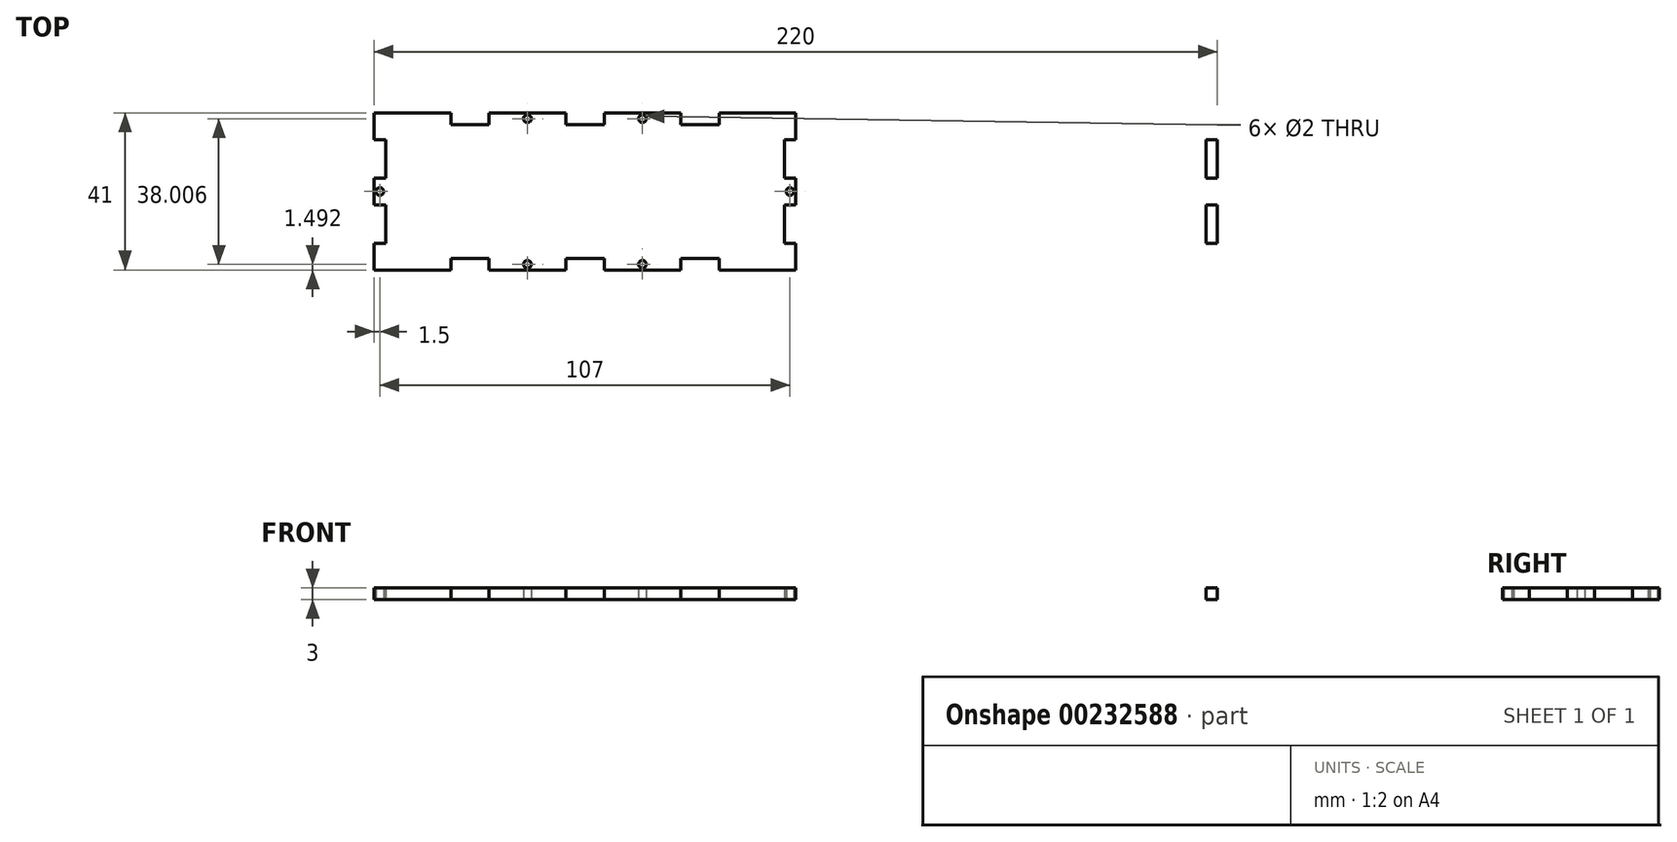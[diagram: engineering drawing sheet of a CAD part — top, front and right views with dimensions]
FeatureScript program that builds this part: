
annotation { "Feature Type Name" : "Feature", "Feature Type Description" : "" }
export const myFeature = defineFeature(function(context is Context, id is Id, definition is map)
    precondition{}
    {
        {
            var Q0;
            Q0=qCreatedBy(makeId("Top.planeOp"),FACE);
            var sketch = newSketch(context, id + "F0", { "sketchPlane" : qUnion([Q0])});
            skLineSegment(sketch, "E0.bottom", {"start": v(-80, 27.46) * mm, "end": v(-60, 27.46) * mm});
            skLineSegment(sketch, "E0.top", {"start": v(-80, -13.54) * mm, "end": v(-60, -13.54) * mm});
            skLineSegment(sketch, "E0.left", {"start": v(-80, 27.46) * mm, "end": v(-80, 20.46) * mm});
            skLineSegment(sketch, "E0.right", {"start": v(30, 27.46) * mm, "end": v(30, 20.46) * mm});
            skLineSegment(sketch, "E1", {"start": v(-80, 20.46) * mm, "end": v(-77, 20.46) * mm});
            skLineSegment(sketch, "E2", {"start": v(-77, 20.46) * mm, "end": v(-77, 10.46) * mm});
            skLineSegment(sketch, "E3", {"start": v(-77, 10.46) * mm, "end": v(-80, 10.46) * mm});
            skLineSegment(sketch, "E4", {"start": v(-80, 10.46) * mm, "end": v(-80, 3.46) * mm});
            skLineSegment(sketch, "E5", {"start": v(-80, 3.46) * mm, "end": v(-77, 3.46) * mm});
            skLineSegment(sketch, "E6", {"start": v(-77, 3.46) * mm, "end": v(-77, -6.54) * mm});
            skLineSegment(sketch, "E7", {"start": v(-77, -6.54) * mm, "end": v(-80, -6.54) * mm});
            skLineSegment(sketch, "E8", {"start": v(-60, 27.46) * mm, "end": v(-60, 24.45) * mm});
            skLineSegment(sketch, "E9", {"start": v(-60, 24.45) * mm, "end": v(-50, 24.45) * mm});
            skLineSegment(sketch, "E10", {"start": v(-50, 24.45) * mm, "end": v(-50, 27.46) * mm});
            skLineSegment(sketch, "E11", {"start": v(-50, 27.46) * mm, "end": v(-30, 27.46) * mm});
            skLineSegment(sketch, "E12", {"start": v(-30, 27.46) * mm, "end": v(-30, 24.46) * mm});
            skLineSegment(sketch, "E13", {"start": v(-30, 24.46) * mm, "end": v(-20, 24.46) * mm});
            skLineSegment(sketch, "E14", {"start": v(-20, 24.46) * mm, "end": v(-20, 27.46) * mm});
            skLineSegment(sketch, "E15", {"start": v(-20, 27.46) * mm, "end": v(0, 27.46) * mm});
            skLineSegment(sketch, "E16", {"start": v(0, 27.46) * mm, "end": v(0, 24.46) * mm});
            skLineSegment(sketch, "E17", {"start": v(0, 24.46) * mm, "end": v(10, 24.46) * mm});
            skLineSegment(sketch, "E18", {"start": v(10, 24.46) * mm, "end": v(10, 27.46) * mm});
            skLineSegment(sketch, "E19.MirrorCS", {"start": v(140, 3.46) * mm, "end": v(137, 3.46) * mm});
            skLineSegment(sketch, "E20.MirrorCS", {"start": v(137, 10.46) * mm, "end": v(140, 10.46) * mm});
            skLineSegment(sketch, "E21.MirrorCS", {"start": v(140, 20.46) * mm, "end": v(137, 20.46) * mm});
            skLineSegment(sketch, "E22.MirrorCS", {"start": v(137, -6.54) * mm, "end": v(140, -6.54) * mm});
            skLineSegment(sketch, "E23.MirrorCS", {"start": v(137, 3.46) * mm, "end": v(137, -6.54) * mm});
            skLineSegment(sketch, "E24.MirrorCS", {"start": v(140, 10.46) * mm, "end": v(140, 3.46) * mm});
            skLineSegment(sketch, "E25.MirrorCS", {"start": v(140, 27.46) * mm, "end": v(140, -13.54) * mm});
            skLineSegment(sketch, "E26.MirrorCS", {"start": v(137, 20.46) * mm, "end": v(137, 10.46) * mm});
            skLineSegment(sketch, "E27.MirrorCS", {"start": v(140, 27.46) * mm, "end": v(140, 20.46) * mm});
            skLineSegment(sketch, "E28", {"start": v(30, 20.46) * mm, "end": v(27, 20.46) * mm});
            skLineSegment(sketch, "E29", {"start": v(27, 20.46) * mm, "end": v(27, 10.46) * mm});
            skLineSegment(sketch, "E30", {"start": v(27, 10.46) * mm, "end": v(30, 10.46) * mm});
            skLineSegment(sketch, "E31", {"start": v(30, 10.46) * mm, "end": v(30, 3.46) * mm});
            skLineSegment(sketch, "E32", {"start": v(30, 3.46) * mm, "end": v(27, 3.46) * mm});
            skLineSegment(sketch, "E33", {"start": v(27, 3.46) * mm, "end": v(27, -6.54) * mm});
            skLineSegment(sketch, "E34", {"start": v(27, -6.54) * mm, "end": v(30, -6.54) * mm});
            skLineSegment(sketch, "E35", {"start": v(30, -13.54) * mm, "end": v(10, -13.54) * mm});
            skLineSegment(sketch, "E36", {"start": v(10, -13.54) * mm, "end": v(10, -10.54) * mm});
            skLineSegment(sketch, "E37", {"start": v(10, -10.54) * mm, "end": v(0, -10.54) * mm});
            skLineSegment(sketch, "E38", {"start": v(0, -10.54) * mm, "end": v(0, -13.54) * mm});
            skLineSegment(sketch, "E39", {"start": v(0, -13.54) * mm, "end": v(-20, -13.54) * mm});
            skLineSegment(sketch, "E40", {"start": v(-20, -13.54) * mm, "end": v(-20, -10.54) * mm});
            skLineSegment(sketch, "E41", {"start": v(-20, -10.54) * mm, "end": v(-30, -10.54) * mm});
            skLineSegment(sketch, "E42", {"start": v(-30, -10.54) * mm, "end": v(-30, -13.54) * mm});
            skLineSegment(sketch, "E43", {"start": v(-60, -10.55) * mm, "end": v(-50, -10.55) * mm});
            skLineSegment(sketch, "E44", {"start": v(-50, -10.55) * mm, "end": v(-50, -13.54) * mm});
            skLineSegment(sketch, "E45", {"start": v(-60, -10.55) * mm, "end": v(-60, -13.54) * mm});
            skLineSegment(sketch, "E46.trimOffspring", {"start": v(10, 27.46) * mm, "end": v(30, 27.46) * mm});
            skLineSegment(sketch, "E47.trimOffspring", {"start": v(30, -6.54) * mm, "end": v(30, -13.54) * mm});
            skLineSegment(sketch, "E48.trimOffspring", {"start": v(10, -13.54) * mm, "end": v(30, -13.54) * mm});
            skLineSegment(sketch, "E49.trimOffspring", {"start": v(-20, -13.54) * mm, "end": v(0, -13.54) * mm});
            skLineSegment(sketch, "E50.trimOffspring", {"start": v(-50, -13.54) * mm, "end": v(-30, -13.54) * mm});
            skLineSegment(sketch, "E51.trimOffspring", {"start": v(-80, -6.54) * mm, "end": v(-80, -13.54) * mm});
            skPoint(sketch, "E52.MirrorCS.start.orphan", {"position": v(-80, 27.46) * mm});
            skCircle(sketch, "E53", {"center": v(-40, 25.95) * mm, "radius": 1 * mm});
            skPoint(sketch, "E53.centerSnap0", {"position": v(-50, 25.95) * mm});
            skPoint(sketch, "E53.centerSnap1", {"position": v(-40, 27.46) * mm});
            skCircle(sketch, "E54", {"center": v(-10, 25.96) * mm, "radius": 1 * mm});
            skPoint(sketch, "E54.centerSnap0", {"position": v(-10, 27.46) * mm});
            skPoint(sketch, "E54.centerSnap1", {"position": v(0, 25.96) * mm});
            skCircle(sketch, "E55", {"center": v(-40, -12.05) * mm, "radius": 1 * mm});
            skPoint(sketch, "E55.centerSnap0", {"position": v(-40, -13.54) * mm});
            skPoint(sketch, "E55.centerSnap1", {"position": v(-50, -12.05) * mm});
            skCircle(sketch, "E56", {"center": v(-10, -12.04) * mm, "radius": 1 * mm});
            skPoint(sketch, "E56.centerSnap0", {"position": v(-10, -13.54) * mm});
            skPoint(sketch, "E56.centerSnap1", {"position": v(-20, -12.04) * mm});
            skPoint(sketch, "E57.centerSnap0", {"position": v(-80, 6.96) * mm});
            skPoint(sketch, "E57.centerSnap1", {"position": v(-78.5, 10.46) * mm});
            skCircle(sketch, "E58", {"center": v(-78.5, 6.96) * mm, "radius": 1 * mm});
            skCircle(sketch, "E59", {"center": v(28.5, 6.96) * mm, "radius": 1 * mm});
            skPoint(sketch, "E59.centerSnap0", {"position": v(28.5, 10.46) * mm});
            skPoint(sketch, "E59.centerSnap1", {"position": v(30, 6.96) * mm});
            skSolve(sketch);
        }
        {
            var Q0;
            Q0 = qSketchRegion(id + "F0", true);
            extrude(context, id + "F1", {"entities" : qUnion([Q0]), "depth" : 3 * mm});
        }
    });
